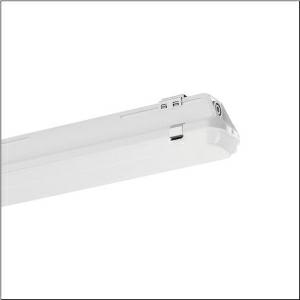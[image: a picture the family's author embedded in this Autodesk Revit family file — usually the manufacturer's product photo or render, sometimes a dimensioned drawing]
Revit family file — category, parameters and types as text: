
# Revit family: monsun_r__11_51fp108p460h_7b9f
name_source: partatom
category: Lighting Fixtures
units: mm (PartAtom-declared; Revit-internal decimal feet)

## family parameters
Cut with Voids When Loaded = No
Host = Face
Light Source = No
Part Type = Normal
Room Calculation Point = No
Round Connector Dimension = Use Diameter
Shared = No

## types (1)
- Monsun® 11 (1 x LED, 6100 lm, 33.9 W, 4000K)
    Apparent Load = 34 VA
    CIE Flux Codes = 47 77 93 94 100
    Color Rendering = 80
    Color Temperature = 4000K
    Default Elevation = 1800 mm
    Description = Monsun® 11, damp-proof luminaire, chain hanger, primary optical cover: enclosure, of PMMA, light emission: direct distribution, primary light characteristic: symmetric, installation type: suspended mounting, surface-mounted, horizontal mounting, vertical mounting, LED, rated luminous flux: 6.100lm, luminous efficacy: 180lm/W, light colour: 840, colour temperature: 4000K, control gear: ON/OFF, with terminal, 3-pole, max. 2.5mm², mains connection: 220..240V, AC, 50/60Hz, rated input power: 34W, luminaire housing, of glass-fibre reinforced polyester, uncoated, bright grey, incl. chain hanger, length: 1.590mm, width: 90mm, height: 88mm, clip for enclosure, of stainless steel (V2A), ceiling mounting element, of stainless steel (V2A), chain hanger, of stainless steel (V2A), protection rating (complete): IP66, insulation class (complete): insulation class I (protective earthing), certification: CE, ENEC, VDE, UKCA, protection symbol: D, impact resistance: IK04, permissible operating ambient temperature: -35..+40°C, standard: EN 50419, EN 60598-2-1, no direct snow, no direct sun, no direct rain, for indoor or canopied outdoor use, corresponds to IFS (International Featured Standards) requirements for safety and quality in the food industry, contact your sales advisor before using the luminaires in applications with unclear chemical exposure, large temperature fluctuations or condensation-forming humidity, LABS conformity tested according to VDMA 24364:2018-05, packaging unit: 1 piece
    Height = 89 mm
    Lamp = 1 x LED
    Lamp Light Flux = 6100 lm
    Lamp Power = 33.9 W
    Lamp count = 1
    Length = 1590 mm
    Luminous efficacy = 180 lm/W
    Manufacturer = Siteco
    ModVariant = No
    Model = 51FP108P460H
    Mounting Place = Ceiling
    Mounting Type = Surface mounted
    Number of Poles = 1
    OnlyDefault = Yes
    Power Factor = 1
    Product Name = Monsun® 11
    Product group = damp-proof luminaire
    ProductGroupID = 301
    Protection Class = Protection class I
    Protection Degree = IP 66
    RLX_Detail_Level = 1
    RLX_Emergency_Light_Flux = 0 lm
    RLX_Emergency_Type = 0
    RLX_Emergency_Type_DB = No
    RlxData = <blob elided: 88533 chars, md5=0195148c>
    Socket = socket
    Standby Power = 0 W
    System Light Flux = 6100 lm
    System Power = 34 W
    Type Comments = Product without accessories
    Type Image = l_1349237.jpg
    URL = http://relux.com
    VarID = ---
    Voltage = 0 V
    Weight = 0.00 kg
    Width = 90 mm

## geometry (parser evidence)
native form markers: Blend x4, Sweep x13
no freeform markers — native parametric forms only
